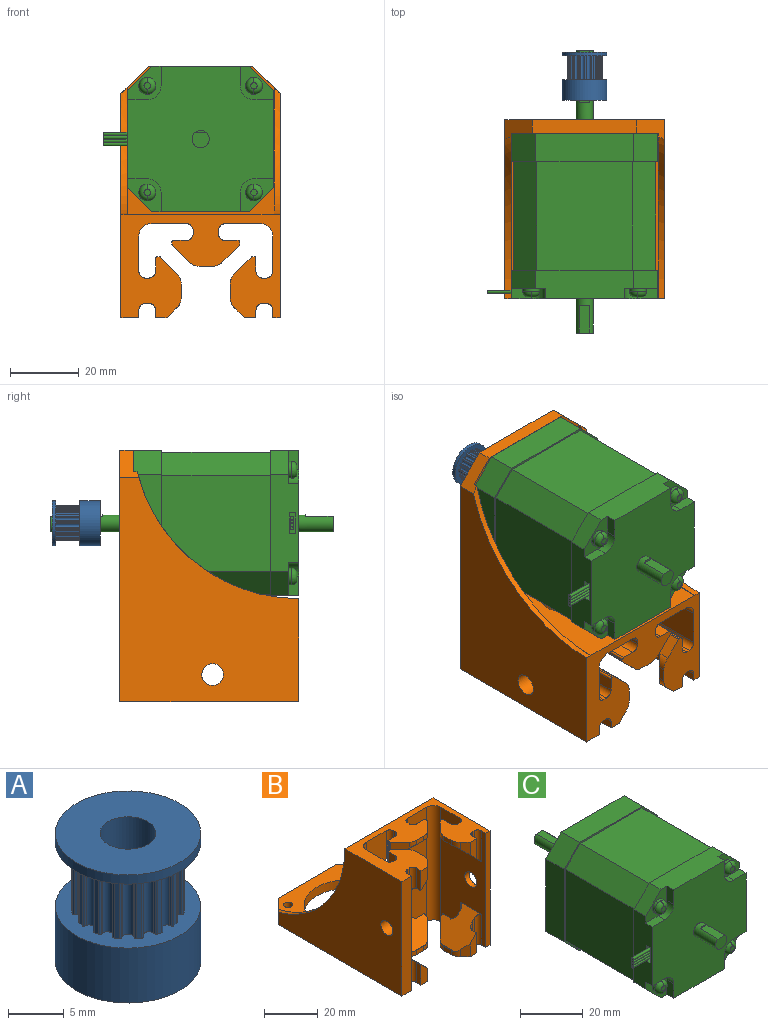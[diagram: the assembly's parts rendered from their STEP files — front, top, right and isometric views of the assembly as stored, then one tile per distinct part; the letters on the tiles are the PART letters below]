
ASSEMBLY  parts=3 mates=2
PART A: 104 faces, bbox 13x13x14 mm
  f0: cylinder r=2.5mm len=14mm, axis (0,0,1), area 214.8mm2, adj f2,f102,f103
  f1: cylinder r=6.5mm len=13mm, axis (0,0,1), area 240.1mm2, adj f2,f3,f103
  f2: plane 13x13mm, normal (0,0,-1), area 113.1mm2, adj f0,f1
  f3: plane 13x13mm, normal (0,0,1), area 62.7mm2, adj f1,f4,f5,f6,f7,f8,f9,f10
  f4: cylinder r=0.15mm len=7mm, axis (0,0,-1), area 1.7mm2, adj f3,f5,f99,f100
  f5: cylinder r=1mm len=7mm, axis (0,0,-1), area 1.7mm2, adj f3,f4,f6,f100
  f6: cylinder r=0.56mm len=7mm, axis (0,0,-1), area 9mm2, adj f3,f5,f7,f100
  f7: cylinder r=1mm len=7mm, axis (0,0,-1), area 1.7mm2, adj f3,f6,f8,f100
  f8: cylinder r=0.15mm len=7mm, axis (0,0,-1), area 1.7mm2, adj f3,f7,f9,f100
  f9: plane 7x0.49mm, normal (0.98,0.2,0), area 3.5mm2, adj f3,f8,f10,f100
  f10: cylinder r=0.15mm len=7mm, axis (0,0,-1), area 1.7mm2, adj f3,f9,f11,f100
  f11: cylinder r=1mm len=7mm, axis (0,0,-1), area 1.7mm2, adj f3,f10,f12,f100
  f12: cylinder r=0.56mm len=7mm, axis (0,0,-1), area 9mm2, adj f3,f11,f13,f100
  f13: cylinder r=1mm len=7mm, axis (0,0,-1), area 1.7mm2, adj f3,f12,f14,f100
  f14: cylinder r=0.15mm len=7mm, axis (0,0,-1), area 1.7mm2, adj f3,f13,f15,f100
  f15: plane 7x0.41mm, normal (0.83,0.56,0), area 3.5mm2, adj f3,f14,f16,f100
  f16: cylinder r=0.15mm len=7mm, axis (0,0,-1), area 1.7mm2, adj f3,f15,f17,f100
  f17: cylinder r=1mm len=7mm, axis (0,0,-1), area 1.7mm2, adj f3,f16,f18,f100
  f18: cylinder r=0.56mm len=7mm, axis (0,0,-1), area 9mm2, adj f3,f17,f19,f100
  f19: cylinder r=1mm len=7mm, axis (0,0,-1), area 1.7mm2, adj f3,f18,f20,f100
  f20: cylinder r=0.15mm len=7mm, axis (0,0,-1), area 1.7mm2, adj f3,f19,f21,f100
  f21: plane 7x0.41mm, normal (0.56,0.83,0), area 3.5mm2, adj f3,f20,f22,f100
  f22: cylinder r=0.15mm len=7mm, axis (0,0,-1), area 1.7mm2, adj f3,f21,f23,f100
  f23: cylinder r=1mm len=7mm, axis (0,0,-1), area 1.7mm2, adj f3,f22,f24,f100
  f24: cylinder r=0.56mm len=7mm, axis (0,0,-1), area 9mm2, adj f3,f23,f25,f100
  f25: cylinder r=1mm len=7mm, axis (0,0,-1), area 1.7mm2, adj f3,f24,f26,f100
  f26: cylinder r=0.15mm len=7mm, axis (0,0,-1), area 1.7mm2, adj f3,f25,f27,f100
  f27: plane 7x0.49mm, normal (0.2,0.98,0), area 3.5mm2, adj f3,f26,f28,f100
  f28: cylinder r=0.15mm len=7mm, axis (0,0,-1), area 1.7mm2, adj f3,f27,f29,f100
  f29: cylinder r=1mm len=7mm, axis (0,0,-1), area 1.7mm2, adj f3,f28,f30,f100
  f30: cylinder r=0.56mm len=7mm, axis (0,0,-1), area 9mm2, adj f3,f29,f31,f100
  f31: cylinder r=1mm len=7mm, axis (0,0,-1), area 1.7mm2, adj f3,f30,f32,f100
  f32: cylinder r=0.15mm len=7mm, axis (0,0,-1), area 1.7mm2, adj f3,f31,f33,f100
  f33: plane 7x0.49mm, normal (-0.2,0.98,0), area 3.5mm2, adj f3,f32,f34,f100
  f34: cylinder r=0.15mm len=7mm, axis (0,0,-1), area 1.7mm2, adj f3,f33,f35,f100
  f35: cylinder r=1mm len=7mm, axis (0,0,-1), area 1.7mm2, adj f3,f34,f36,f100
  f36: cylinder r=0.56mm len=7mm, axis (0,0,-1), area 9mm2, adj f3,f35,f37,f100
  f37: cylinder r=1mm len=7mm, axis (0,0,-1), area 1.7mm2, adj f3,f36,f38,f100
  f38: cylinder r=0.15mm len=7mm, axis (0,0,-1), area 1.7mm2, adj f3,f37,f39,f100
  f39: plane 7x0.41mm, normal (-0.56,0.83,0), area 3.5mm2, adj f3,f38,f40,f100
  f40: cylinder r=0.15mm len=7mm, axis (0,0,-1), area 1.7mm2, adj f3,f39,f41,f100
  f41: cylinder r=1mm len=7mm, axis (0,0,-1), area 1.7mm2, adj f3,f40,f42,f100
  f42: cylinder r=0.56mm len=7mm, axis (0,0,-1), area 9mm2, adj f3,f41,f43,f100
  f43: cylinder r=1mm len=7mm, axis (0,0,-1), area 1.7mm2, adj f3,f42,f44,f100
  f44: cylinder r=0.15mm len=7mm, axis (0,0,-1), area 1.7mm2, adj f3,f43,f45,f100
  f45: plane 7x0.41mm, normal (-0.83,0.56,0), area 3.5mm2, adj f3,f44,f46,f100
  f46: cylinder r=0.15mm len=7mm, axis (0,0,-1), area 1.7mm2, adj f3,f45,f47,f100
  f47: cylinder r=1mm len=7mm, axis (0,0,-1), area 1.7mm2, adj f3,f46,f48,f100
  f48: cylinder r=0.56mm len=7mm, axis (0,0,-1), area 9mm2, adj f3,f47,f49,f100
  f49: cylinder r=1mm len=7mm, axis (0,0,-1), area 1.7mm2, adj f3,f48,f50,f100
  f50: cylinder r=0.15mm len=7mm, axis (0,0,-1), area 1.7mm2, adj f3,f49,f51,f100
  f51: plane 7x0.49mm, normal (-0.98,0.2,0), area 3.5mm2, adj f3,f50,f52,f100
  f52: cylinder r=0.15mm len=7mm, axis (0,0,-1), area 1.7mm2, adj f3,f51,f53,f100
  f53: cylinder r=1mm len=7mm, axis (0,0,-1), area 1.7mm2, adj f3,f52,f54,f100
  f54: cylinder r=0.56mm len=7mm, axis (0,0,-1), area 9mm2, adj f3,f53,f55,f100
  f55: cylinder r=1mm len=7mm, axis (0,0,-1), area 1.7mm2, adj f3,f54,f56,f100
  f56: cylinder r=0.15mm len=7mm, axis (0,0,-1), area 1.7mm2, adj f3,f55,f57,f100
  f57: plane 7x0.49mm, normal (-0.98,-0.2,0), area 3.5mm2, adj f3,f56,f58,f100
  f58: cylinder r=0.15mm len=7mm, axis (0,0,-1), area 1.7mm2, adj f3,f57,f59,f100
  f59: cylinder r=1mm len=7mm, axis (0,0,-1), area 1.7mm2, adj f3,f58,f60,f100
  f60: cylinder r=0.56mm len=7mm, axis (0,0,-1), area 9mm2, adj f3,f59,f61,f100
  f61: cylinder r=1mm len=7mm, axis (0,0,-1), area 1.7mm2, adj f3,f60,f62,f100
  f62: cylinder r=0.15mm len=7mm, axis (0,0,-1), area 1.7mm2, adj f3,f61,f63,f100
  f63: plane 7x0.41mm, normal (-0.83,-0.56,0), area 3.5mm2, adj f3,f62,f64,f100
  f64: cylinder r=0.15mm len=7mm, axis (0,0,-1), area 1.7mm2, adj f3,f63,f65,f100
  f65: cylinder r=1mm len=7mm, axis (0,0,-1), area 1.7mm2, adj f3,f64,f66,f100
  f66: cylinder r=0.56mm len=7mm, axis (0,0,-1), area 9mm2, adj f3,f65,f67,f100
  f67: cylinder r=1mm len=7mm, axis (0,0,-1), area 1.7mm2, adj f3,f66,f68,f100
  f68: cylinder r=0.15mm len=7mm, axis (0,0,-1), area 1.7mm2, adj f3,f67,f69,f100
  f69: plane 7x0.41mm, normal (-0.56,-0.83,0), area 3.5mm2, adj f3,f68,f70,f100
  f70: cylinder r=0.15mm len=7mm, axis (0,0,-1), area 1.7mm2, adj f3,f69,f71,f100
  f71: cylinder r=1mm len=7mm, axis (0,0,-1), area 1.7mm2, adj f3,f70,f72,f100
  f72: cylinder r=0.56mm len=7mm, axis (0,0,-1), area 9mm2, adj f3,f71,f73,f100
  f73: cylinder r=1mm len=7mm, axis (0,0,-1), area 1.7mm2, adj f3,f72,f74,f100
  f74: cylinder r=0.15mm len=7mm, axis (0,0,-1), area 1.7mm2, adj f3,f73,f75,f100
  f75: plane 7x0.49mm, normal (-0.2,-0.98,0), area 3.5mm2, adj f3,f74,f76,f100
  f76: cylinder r=0.15mm len=7mm, axis (0,0,-1), area 1.7mm2, adj f3,f75,f77,f100
  f77: cylinder r=1mm len=7mm, axis (0,0,-1), area 1.7mm2, adj f3,f76,f78,f100
  f78: cylinder r=0.56mm len=7mm, axis (0,0,-1), area 9mm2, adj f3,f77,f79,f100
  f79: cylinder r=1mm len=7mm, axis (0,0,-1), area 1.7mm2, adj f3,f78,f80,f100
  f80: cylinder r=0.15mm len=7mm, axis (0,0,-1), area 1.7mm2, adj f3,f79,f81,f100
  f81: plane 7x0.49mm, normal (0.2,-0.98,0), area 3.5mm2, adj f3,f80,f82,f100
  f82: cylinder r=0.15mm len=7mm, axis (0,0,-1), area 1.7mm2, adj f3,f81,f83,f100
  f83: cylinder r=1mm len=7mm, axis (0,0,-1), area 1.7mm2, adj f3,f82,f84,f100
  f84: cylinder r=0.56mm len=7mm, axis (0,0,-1), area 9mm2, adj f3,f83,f85,f100
  f85: cylinder r=1mm len=7mm, axis (0,0,-1), area 1.7mm2, adj f3,f84,f86,f100
  f86: cylinder r=0.15mm len=7mm, axis (0,0,-1), area 1.7mm2, adj f3,f85,f87,f100
  f87: plane 7x0.41mm, normal (0.56,-0.83,0), area 3.5mm2, adj f3,f86,f88,f100
  f88: cylinder r=0.15mm len=7mm, axis (0,0,-1), area 1.7mm2, adj f3,f87,f89,f100
  f89: cylinder r=1mm len=7mm, axis (0,0,-1), area 1.7mm2, adj f3,f88,f90,f100
  f90: cylinder r=0.56mm len=7mm, axis (0,0,-1), area 9mm2, adj f3,f89,f91,f100
  f91: cylinder r=1mm len=7mm, axis (0,0,-1), area 1.7mm2, adj f3,f90,f92,f100
  f92: cylinder r=0.15mm len=7mm, axis (0,0,-1), area 1.7mm2, adj f3,f91,f93,f100
  f93: plane 7x0.41mm, normal (0.83,-0.56,0), area 3.5mm2, adj f3,f92,f94,f100
  f94: cylinder r=0.15mm len=7mm, axis (0,0,-1), area 1.7mm2, adj f3,f93,f95,f100
  f95: cylinder r=1mm len=7mm, axis (0,0,-1), area 1.7mm2, adj f3,f94,f96,f100
  f96: cylinder r=0.56mm len=7mm, axis (0,0,-1), area 9mm2, adj f3,f95,f97,f100
  f97: cylinder r=1mm len=7mm, axis (0,0,-1), area 1.7mm2, adj f3,f96,f98,f100
  f98: cylinder r=0.15mm len=7mm, axis (0,0,-1), area 1.7mm2, adj f3,f97,f99,f100
  f99: plane 7x0.49mm, normal (0.98,-0.2,0), area 3.5mm2, adj f3,f4,f98,f100
  f100: plane 13x13mm, normal (0,0,-1), area 62.7mm2, adj f4,f5,f6,f7,f8,f9,f10,f11
  f101: cylinder r=6.5mm len=13mm, axis (0,0,-1), area 40.8mm2, adj f100,f102
  f102: plane 13x13mm, normal (0,0,1), area 113.1mm2, adj f0,f101
  f103: cylinder r=1.25mm len=4.34mm, axis (0,-1,0), area 32.2mm2, adj f0,f1
PART B: 154 faces, bbox 46.4x73.1x52.1 mm
  f0: plane 52x10.23mm, normal (0,-1,0), area 397.5mm2, adj f41,f42,f43,f111,f125,f144,f145,f148
  f1: plane 9.14x3.34mm, normal (0,-1,0), area 24.9mm2, adj f91,f101,f111,f137
  f2: plane 9.14x3.34mm, normal (0,-1,0), area 24.9mm2, adj f92,f102,f125,f139
  f3: plane 9.14x3.34mm, normal (0,-1,0), area 24.9mm2, adj f89,f99,f111,f136
  f4: plane 9.14x3.34mm, normal (0,-1,0), area 24.9mm2, adj f90,f100,f125,f141
  f5: cylinder r=1.95mm len=14mm, axis (0,0,-1), area 40.8mm2, adj f7,f111,f117,f138
  f6: cylinder r=1.95mm len=14mm, axis (0,0,-1), area 40.8mm2, adj f8,f117,f125,f140
  f7: plane 12.05x0.96mm, normal (1,0,0), area 11.1mm2, adj f5,f9,f111,f138
  f8: plane 12.05x0.96mm, normal (1,0,0), area 11.1mm2, adj f6,f10,f125,f140
  f9: cylinder r=1.95mm len=11.09mm, axis (0,0,-1), area 30.2mm2, adj f7,f11,f111,f138
  f10: cylinder r=1.95mm len=11.09mm, axis (0,0,-1), area 30.2mm2, adj f8,f12,f125,f140
  f11: plane 9.14x3.77mm, normal (0,1,0), area 34.4mm2, adj f9,f13,f111,f138
  f12: plane 9.14x3.77mm, normal (0,1,0), area 34.4mm2, adj f10,f14,f125,f140
  f13: cylinder r=0.5mm len=9.14mm, axis (0,0,-1), area 7.1mm2, adj f11,f15,f111,f138
  f14: cylinder r=0.5mm len=9.14mm, axis (0,0,-1), area 7.1mm2, adj f12,f16,f125,f140
  f15: plane 8.63x0.53mm, normal (1,0,0), area 4.5mm2, adj f13,f17,f111,f138
  f16: plane 8.63x0.53mm, normal (1,0,0), area 4.5mm2, adj f14,f18,f125,f140
  f17: cylinder r=0.5mm len=8.1mm, axis (0,0,-1), area 3.1mm2, adj f15,f19,f111,f138
  f18: cylinder r=0.5mm len=8.1mm, axis (0,0,-1), area 3.1mm2, adj f16,f20,f125,f140
  f19: plane 7.75x5.05mm, normal (0.71,-0.71,0), area 37.3mm2, adj f17,f21,f111,f138
  f20: plane 7.75x5.05mm, normal (0.71,-0.71,0), area 37.3mm2, adj f18,f22,f125,f140
  f21: cylinder r=4.36mm len=2.78mm, axis (0,0,-1), area 6.5mm2, adj f19,f23,f111,f134,f138
  f22: cylinder r=4.36mm len=2.78mm, axis (0,0,-1), area 6.5mm2, adj f20,f24,f125,f135,f140
  f23: plane 3.8x2mm, normal (0,-1,0), area 7.6mm2, adj f21,f25,f111,f134
  f24: plane 3.8x2mm, normal (0,-1,0), area 7.6mm2, adj f22,f26,f125,f135
  f25: cylinder r=4.36mm len=2.78mm, axis (0,0,-1), area 6.5mm2, adj f23,f27,f111,f134,f138
  f26: cylinder r=4.36mm len=2.78mm, axis (0,0,-1), area 6.5mm2, adj f24,f28,f125,f135,f140
  f27: plane 7.75x5.05mm, normal (-0.71,-0.71,0), area 37.3mm2, adj f25,f29,f111,f138
  f28: plane 7.75x5.05mm, normal (-0.71,-0.71,0), area 37.3mm2, adj f26,f30,f125,f140
  f29: cylinder r=0.5mm len=8.1mm, axis (0,0,-1), area 3.1mm2, adj f27,f31,f111,f138
  f30: cylinder r=0.5mm len=8.1mm, axis (0,0,-1), area 3.1mm2, adj f28,f32,f125,f140
  f31: plane 8.63x0.53mm, normal (-1,0,0), area 4.5mm2, adj f29,f33,f111,f138
  f32: plane 8.63x0.53mm, normal (-1,0,0), area 4.5mm2, adj f30,f34,f125,f140
  f33: cylinder r=0.5mm len=9.14mm, axis (0,0,-1), area 7.1mm2, adj f31,f35,f111,f138
  f34: cylinder r=0.5mm len=9.14mm, axis (0,0,-1), area 7.1mm2, adj f32,f36,f125,f140
  f35: plane 9.14x3.77mm, normal (0,1,0), area 34.4mm2, adj f33,f37,f111,f138
  f36: plane 9.14x3.77mm, normal (0,1,0), area 34.4mm2, adj f34,f38,f125,f140
  f37: cylinder r=1.95mm len=11.09mm, axis (0,0,-1), area 30.2mm2, adj f35,f39,f111,f138
  f38: cylinder r=1.95mm len=11.09mm, axis (0,0,-1), area 30.2mm2, adj f36,f40,f125,f140
  f39: plane 12.05x0.96mm, normal (-1,0,0), area 11.1mm2, adj f37,f41,f111,f138
  f40: plane 11.18x0.96mm, normal (-1,0,0), area 10.7mm2, adj f38,f42,f125,f140,f149
  f41: cylinder r=1.95mm len=13.8mm, axis (0,0,-1), area 38.8mm2, adj f0,f39,f111,f138,f144,f151
  f42: cylinder r=1.95mm len=12.8mm, axis (0,0,-1), area 35.8mm2, adj f0,f40,f125,f145,f149
  f43: cylinder r=3.49mm len=52mm, axis (0,0,-1), area 296.8mm2, adj f0,f111,f118,f125
  f44: cylinder r=1.95mm len=14mm, axis (0,0,-1), area 40.8mm2, adj f46,f111,f118,f136
  f45: cylinder r=1.95mm len=14mm, axis (0,0,-1), area 40.8mm2, adj f47,f118,f125,f141
  f46: plane 12.05x0.96mm, normal (0,1,0), area 11.1mm2, adj f44,f48,f111,f136
  f47: plane 12.05x0.96mm, normal (0,1,0), area 11.1mm2, adj f45,f49,f125,f141
  f48: cylinder r=1.95mm len=11.09mm, axis (0,0,-1), area 30.2mm2, adj f46,f50,f111,f136
  f49: cylinder r=1.95mm len=11.09mm, axis (0,0,-1), area 30.2mm2, adj f47,f51,f125,f141
  f50: plane 9.14x3.77mm, normal (-1,0,0), area 34.4mm2, adj f48,f52,f111,f136
  f51: plane 9.14x3.77mm, normal (-1,0,0), area 34.4mm2, adj f49,f53,f125,f141
  f52: cylinder r=0.5mm len=9.14mm, axis (0,0,-1), area 7.1mm2, adj f50,f54,f111,f136
  f53: cylinder r=0.5mm len=9.14mm, axis (0,0,-1), area 7.1mm2, adj f51,f55,f125,f141
  f54: plane 8.63x0.57mm, normal (0,1,0), area 4.7mm2, adj f52,f56,f111,f136
  f55: plane 8.63x0.57mm, normal (0,1,0), area 4.7mm2, adj f53,f57,f125,f141
  f56: cylinder r=0.5mm len=8.07mm, axis (0,0,-1), area 3.1mm2, adj f54,f58,f111,f136
  f57: cylinder r=0.5mm len=8.07mm, axis (0,0,-1), area 3.1mm2, adj f55,f59,f125,f141
  f58: plane 7.71x5.01mm, normal (0.71,0.71,0), area 36.9mm2, adj f56,f60,f111,f136
  f59: plane 7.71x5.01mm, normal (0.71,0.71,0), area 36.9mm2, adj f57,f61,f125,f141
  f60: cylinder r=4.37mm len=2.79mm, axis (0,0,-1), area 6.5mm2, adj f58,f62,f111,f132,f136
  f61: cylinder r=4.37mm len=2.79mm, axis (0,0,-1), area 6.5mm2, adj f59,f63,f125,f133,f141
  f62: plane 3.87x2mm, normal (1,0,0), area 7.7mm2, adj f60,f64,f111,f132
  f63: plane 3.87x2mm, normal (1,0,0), area 7.7mm2, adj f61,f65,f125,f133
  f64: cylinder r=4.37mm len=3.36mm, axis (0,0,-1), area 8.9mm2, adj f62,f89,f111,f132,f136
  f65: cylinder r=4.37mm len=3.36mm, axis (0,0,-1), area 8.9mm2, adj f63,f90,f125,f133,f141
  f66: cylinder r=4.37mm len=3.36mm, axis (0,0,-1), area 8.9mm2, adj f68,f91,f111,f130,f137
  f67: cylinder r=4.37mm len=3.36mm, axis (0,0,-1), area 8.9mm2, adj f69,f92,f125,f131,f139
  f68: plane 3.87x2mm, normal (-1,0,0), area 7.7mm2, adj f66,f70,f111,f130
  f69: plane 3.87x2mm, normal (-1,0,0), area 7.7mm2, adj f67,f71,f125,f131
  f70: cylinder r=4.37mm len=3.36mm, axis (0,0,-1), area 8.9mm2, adj f68,f72,f111,f130,f137
  f71: cylinder r=4.37mm len=3.36mm, axis (0,0,-1), area 8.9mm2, adj f69,f73,f125,f131,f139
  f72: plane 7.71x4.45mm, normal (-0.71,0.71,0), area 34.5mm2, adj f70,f74,f111,f137
  f73: plane 7.71x4.45mm, normal (-0.71,0.71,0), area 34.5mm2, adj f71,f75,f125,f139
  f74: cylinder r=0.5mm len=8.07mm, axis (0,0,-1), area 3.1mm2, adj f72,f76,f111,f137
  f75: cylinder r=0.5mm len=8.07mm, axis (0,0,-1), area 3.1mm2, adj f73,f77,f125,f139
  f76: plane 8.63x0.57mm, normal (0,1,0), area 4.7mm2, adj f74,f78,f111,f137
  f77: plane 8.63x0.57mm, normal (0,1,0), area 4.7mm2, adj f75,f79,f125,f139
  f78: cylinder r=0.5mm len=9.14mm, axis (0,0,-1), area 7.1mm2, adj f76,f80,f111,f137
  f79: cylinder r=0.5mm len=9.14mm, axis (0,0,-1), area 7.1mm2, adj f77,f81,f125,f139
  f80: plane 9.14x3.77mm, normal (1,0,0), area 34.4mm2, adj f78,f82,f111,f137
  f81: plane 9.14x3.77mm, normal (1,0,0), area 34.4mm2, adj f79,f83,f125,f139
  f82: cylinder r=1.95mm len=11.09mm, axis (0,0,-1), area 30.2mm2, adj f80,f84,f111,f137
  f83: cylinder r=1.95mm len=11.09mm, axis (0,0,-1), area 30.2mm2, adj f81,f85,f125,f139
  f84: plane 12.05x0.96mm, normal (0,1,0), area 11.1mm2, adj f82,f86,f111,f137
  f85: plane 12.05x0.96mm, normal (0,1,0), area 11.1mm2, adj f83,f87,f125,f139
  f86: cylinder r=1.95mm len=14mm, axis (0,0,-1), area 40.8mm2, adj f84,f111,f119,f137
  f87: cylinder r=1.95mm len=14mm, axis (0,0,-1), area 40.8mm2, adj f85,f119,f125,f139
  f88: cylinder r=3.49mm len=52mm, axis (0,0,-1), area 296.8mm2, adj f111,f117,f119,f125
  f89: plane 5.8x2.53mm, normal (0.71,-0.71,0), area 16.2mm2, adj f3,f64,f111,f136
  f90: plane 5.8x2.53mm, normal (0.71,-0.71,0), area 16.2mm2, adj f4,f65,f125,f141
  f91: plane 5.8x2.53mm, normal (-0.71,-0.71,0), area 16.2mm2, adj f1,f66,f111,f137
  f92: plane 5.8x2.53mm, normal (-0.71,-0.71,0), area 16.2mm2, adj f2,f67,f125,f139
  f93: cylinder r=1.95mm len=11.09mm, axis (0,0,-1), area 30.2mm2, adj f95,f99,f111,f136
  f94: cylinder r=1.95mm len=11.09mm, axis (0,0,-1), area 30.2mm2, adj f96,f100,f125,f141
  f95: plane 12.05x0.96mm, normal (0,-1,0), area 11.1mm2, adj f93,f97,f111,f136
  f96: plane 12.05x0.96mm, normal (0,-1,0), area 11.1mm2, adj f94,f98,f125,f141
  f97: cylinder r=1.95mm len=14mm, axis (0,0,-1), area 40.8mm2, adj f95,f111,f118,f136
  f98: cylinder r=1.95mm len=14mm, axis (0,0,-1), area 40.8mm2, adj f96,f118,f125,f141
  f99: plane 9.14x2.21mm, normal (-1,0,0), area 20.2mm2, adj f3,f93,f111,f136
  f100: plane 9.14x2.21mm, normal (-1,0,0), area 20.2mm2, adj f4,f94,f125,f141
  f101: plane 9.14x2.21mm, normal (1,0,0), area 20.2mm2, adj f1,f103,f111,f137
  f102: plane 9.14x2.21mm, normal (1,0,0), area 20.2mm2, adj f2,f104,f125,f139
  f103: cylinder r=1.95mm len=11.09mm, axis (0,0,-1), area 30.2mm2, adj f101,f105,f111,f137
  f104: cylinder r=1.95mm len=11.09mm, axis (0,0,-1), area 30.2mm2, adj f102,f106,f125,f139
  f105: plane 12.05x0.96mm, normal (0,-1,0), area 11.1mm2, adj f103,f107,f111,f137
  f106: plane 12.05x0.96mm, normal (0,-1,0), area 11.1mm2, adj f104,f108,f125,f139
  f107: cylinder r=1.95mm len=14mm, axis (0,0,-1), area 40.8mm2, adj f105,f111,f119,f137
  f108: cylinder r=1.95mm len=14mm, axis (0,0,-1), area 40.8mm2, adj f106,f119,f125,f139
  f109: plane 48x42.7mm, normal (0,1,0), area 1547.3mm2, adj f110,f125,f127,f129,f144,f145,f146,f147
  f110: plane 43.08x42.7mm, normal (0,0,1), area 960.3mm2, adj f109,f115,f120,f121,f122,f123,f124,f127
  f111: plane 73x46.3mm, normal (0,0,-1), area 1851.5mm2, adj f0,f1,f3,f5,f7,f9,f11,f13
  f112: plane 52x2.2mm, normal (0,-1,0), area 114.4mm2, adj f111,f114,f119,f125
  f113: plane 52x5.2mm, normal (0,-1,0), area 270.4mm2, adj f111,f116,f118,f125
  f114: plane 65x52mm, normal (1,0,0), area 2147mm2, adj f111,f112,f125,f126,f143,f152
  f115: plane 30.3x4mm, normal (0,1,0), area 121.2mm2, adj f110,f111,f142,f143
  f116: plane 65x52mm, normal (-1,0,0), area 2147mm2, adj f111,f113,f125,f128,f142,f153
  f117: plane 52x13.06mm, normal (0,-1,0), area 470.1mm2, adj f5,f6,f88,f111,f125,f138,f140,f146
  f118: plane 52x23.67mm, normal (1,0,0), area 884.7mm2, adj f43,f44,f45,f97,f98,f111,f113,f125
  f119: plane 52x23.67mm, normal (-1,0,0), area 884.7mm2, adj f86,f87,f88,f107,f108,f111,f112,f125
  f120: cylinder r=16mm len=32mm, axis (0,0,1), area 402.1mm2, adj f110,f111
  f121: cylinder r=1.7mm len=4mm, axis (0,0,1), area 42.7mm2, adj f110,f111
  f122: cylinder r=1.7mm len=4mm, axis (0,0,1), area 42.7mm2, adj f110,f111
  f123: cylinder r=1.7mm len=4mm, axis (0,0,1), area 42.7mm2, adj f110,f111
  f124: cylinder r=1.7mm len=4mm, axis (0,0,1), area 42.7mm2, adj f110,f111
  f125: plane 46.3x29.92mm, normal (0,0,1), area 761.6mm2, adj f0,f2,f4,f6,f8,f10,f12,f14
  f126: cylinder r=48.28mm len=46.92mm, axis (1,0,0), area 114.1mm2, adj f114,f125,f127,f143
  f127: plane 48x36.88mm, normal (-1,0,0), area 484.7mm2, adj f109,f110,f126,f143
  f128: cylinder r=48.28mm len=46.92mm, axis (-1,0,0), area 114.1mm2, adj f116,f125,f129,f142
  f129: plane 48x36.88mm, normal (1,0,0), area 484.7mm2, adj f109,f110,f128,f142
  f130: plane 7.11x0.31mm, normal (0,0,1), area 1.9mm2, adj f66,f68,f70,f137
  f131: plane 7.11x0.31mm, normal (0,0,-1), area 1.9mm2, adj f67,f69,f71,f139
  f132: plane 7.11x0.31mm, normal (0,0,1), area 1.9mm2, adj f60,f62,f64,f136
  f133: plane 7.11x0.31mm, normal (0,0,-1), area 1.9mm2, adj f61,f63,f65,f141
  f134: plane 7.04x0.31mm, normal (0,0,1), area 1.9mm2, adj f21,f23,f25,f138
  f135: plane 7.04x0.31mm, normal (0,0,-1), area 1.9mm2, adj f22,f24,f26,f140
  f136: plane 17.8x12.09mm, normal (0.71,0,0.71), area 198.9mm2, adj f3,f44,f46,f48,f50,f52,f54,f56
  f137: plane 17.74x12.03mm, normal (-0.71,0,0.71), area 198.9mm2, adj f1,f66,f70,f72,f74,f76,f78,f80
  f138: plane 19.87x12.09mm, normal (0,-0.71,0.71), area 187.4mm2, adj f5,f7,f9,f11,f13,f15,f17,f19
  f139: plane 17.74x12.03mm, normal (-0.71,0,-0.71), area 198.9mm2, adj f2,f67,f71,f73,f75,f77,f79,f81
  f140: plane 19.87x12.09mm, normal (0,-0.71,-0.71), area 177.7mm2, adj f6,f8,f10,f12,f14,f16,f18,f20
  f141: plane 17.8x12.09mm, normal (0.71,0,-0.71), area 198.9mm2, adj f4,f45,f47,f49,f51,f53,f55,f57
  f142: plane 8x8mm, normal (-0.71,0.71,0), area 48.6mm2, adj f110,f111,f115,f116,f128,f129
  f143: plane 8x8mm, normal (0.71,0.71,0), area 48.6mm2, adj f110,f111,f114,f115,f126,f127
  f144: plane 9.82x8.42mm, normal (0.76,0,0.65), area 34.3mm2, adj f0,f41,f109,f148,f151
  f145: plane 9.82x8.42mm, normal (0.76,0,-0.65), area 34.3mm2, adj f0,f42,f109,f148,f149
  f146: plane 9.82x8.41mm, normal (-0.76,0,-0.65), area 35.9mm2, adj f109,f117,f140,f149,f150
  f147: plane 9.82x8.41mm, normal (-0.76,0,0.65), area 34.5mm2, adj f109,f117,f138,f150,f151
  f148: cylinder r=5mm len=6.51mm, axis (0,-1,0), area 18.8mm2, adj f0,f109,f144,f145
  f149: cylinder r=5mm len=7.59mm, axis (0,-1,0), area 42.6mm2, adj f40,f42,f109,f140,f145,f146
  f150: cylinder r=5mm len=6.51mm, axis (0,-1,0), area 18.8mm2, adj f109,f117,f146,f147
  f151: cylinder r=5mm len=7.59mm, axis (0,-1,0), area 36mm2, adj f41,f109,f138,f144,f147
  f152: cylinder r=3.17mm len=6.35mm, axis (-1,0,0), area 43.9mm2, adj f114,f119
  f153: cylinder r=3.17mm len=6.35mm, axis (-1,0,0), area 103.7mm2, adj f116,f118
PART C: 93 faces, bbox 49.3x82x42.3 mm
  f0: plane 42.3x42.3mm, normal (0,1,0), area 858.8mm2, adj f1,f13,f15,f17,f19,f21,f32,f34
  f1: plane 8.25x7mm, normal (0.71,0,0.71), area 81.7mm2, adj f0,f3,f21,f34
  f2: plane 7x7mm, normal (0.71,0,0.71), area 52mm2, adj f12,f22,f23,f35
  f3: plane 42.3x42.3mm, normal (0,-1,0), area 75.6mm2, adj f1,f4,f5,f6,f7,f8,f9,f10
  f4: plane 31.5x6.71mm, normal (0.71,0,0.71), area 298.8mm2, adj f3,f5,f11,f12
  f5: plane 31.5x27.89mm, normal (1,0,0), area 878.4mm2, adj f3,f4,f6,f12
  f6: plane 31.5x6.71mm, normal (0.71,0,-0.71), area 298.8mm2, adj f3,f5,f7,f12
  f7: plane 31.5x27.89mm, normal (0,0,-1), area 878.4mm2, adj f3,f6,f8,f12
  f8: plane 31.5x6.71mm, normal (-0.71,0,-0.71), area 298.8mm2, adj f3,f7,f9,f12
  f9: plane 31.5x27.89mm, normal (-1,0,0), area 878.4mm2, adj f3,f8,f10,f12
  f10: plane 31.5x6.71mm, normal (-0.71,0,0.71), area 298.8mm2, adj f3,f9,f11,f12
  f11: plane 31.5x27.89mm, normal (0,0,1), area 878.4mm2, adj f3,f4,f10,f12
  f12: plane 42.3x42.3mm, normal (0,1,0), area 75.6mm2, adj f2,f4,f5,f6,f7,f8,f9,f10
  f13: plane 28.3x8.25mm, normal (-1,0,0), area 233.5mm2, adj f0,f3,f15,f32
  f14: plane 28.3x8.25mm, normal (-1,0,0), area 207.1mm2, adj f12,f16,f27,f29,f31,f33,f49,f50
  f15: plane 8.25x7mm, normal (-0.71,0,-0.71), area 81.7mm2, adj f0,f3,f13,f17
  f16: plane 7x7mm, normal (-0.71,0,-0.71), area 52mm2, adj f12,f14,f18,f49
  f17: plane 28.3x8.25mm, normal (0,0,-1), area 233.5mm2, adj f0,f3,f15,f19
  f18: plane 28.3x8.25mm, normal (0,0,-1), area 217.6mm2, adj f12,f16,f20,f27,f41,f42,f48,f49
  f19: plane 8.25x7mm, normal (0.71,0,-0.71), area 81.7mm2, adj f0,f3,f17,f21
  f20: plane 7x7mm, normal (0.71,0,-0.71), area 52mm2, adj f12,f18,f22,f41
  f21: plane 28.3x8.25mm, normal (1,0,0), area 233.5mm2, adj f0,f1,f3,f19
  f22: plane 28.3x8.25mm, normal (1,0,0), area 217.6mm2, adj f2,f12,f20,f23,f26,f27,f40,f41
  f23: plane 9.65x9.65mm, normal (0,-1,0), area 46.4mm2, adj f2,f22,f24,f25,f26,f35,f60
  f24: plane 5.65x3mm, normal (1,0,0), area 17mm2, adj f23,f25,f27,f35
  f25: cylinder r=4mm len=4mm, axis (0,1,0), area 18.8mm2, adj f23,f24,f26,f27
  f26: plane 5.65x3mm, normal (0,0,1), area 17mm2, adj f22,f23,f25,f27
  f27: plane 42.3x42.3mm, normal (0,-1,0), area 1410.9mm2, adj f14,f18,f22,f24,f25,f26,f28,f30
  f28: plane 5.65x3mm, normal (-1,0,0), area 17mm2, adj f27,f29,f30,f35
  f29: plane 9.65x9.65mm, normal (0,-1,0), area 46.4mm2, adj f14,f28,f30,f31,f33,f35,f36
  f30: cylinder r=4mm len=4mm, axis (0,-1,0), area 18.8mm2, adj f27,f28,f29,f31
  f31: plane 5.65x3mm, normal (0,0,1), area 17mm2, adj f14,f27,f29,f30
  f32: plane 8.25x7mm, normal (-0.71,0,0.71), area 81.7mm2, adj f0,f3,f13,f34
  f33: plane 7x7mm, normal (-0.71,0,0.71), area 52mm2, adj f12,f14,f29,f35
  f34: plane 28.3x8.25mm, normal (0,0,1), area 233.5mm2, adj f0,f1,f3,f32
  f35: plane 28.3x8.25mm, normal (0,0,1), area 217.6mm2, adj f2,f12,f23,f24,f27,f28,f29,f33
  f36: cylinder r=2.45mm len=4.9mm, axis (0,-1,0), area 15.4mm2, adj f29,f37,f39
  f37: torus R=0.95mm, axis (0,-1,0), area 14.1mm2, adj f36,f38,f39
  f38: plane 1.9x1.9mm, normal (0,-1,0), area 2.8mm2, adj f37,f39
  f39: torus R=0.95mm, axis (0,-1,0), area 14.1mm2, adj f36,f37,f38
  f40: plane 5.65x3mm, normal (0,0,-1), area 17mm2, adj f22,f27,f41,f43
  f41: plane 9.65x9.65mm, normal (0,-1,0), area 46.4mm2, adj f18,f20,f22,f40,f42,f43,f44
  f42: plane 5.65x3mm, normal (1,0,0), area 17mm2, adj f18,f27,f41,f43
  f43: cylinder r=4mm len=4mm, axis (0,-1,0), area 18.8mm2, adj f27,f40,f41,f42
  f44: cylinder r=2.45mm len=4.9mm, axis (0,-1,0), area 15.4mm2, adj f41,f45,f47
  f45: torus R=0.95mm, axis (0,-1,0), area 14.1mm2, adj f44,f46,f47
  f46: plane 1.9x1.9mm, normal (0,-1,0), area 2.8mm2, adj f45,f47
  f47: torus R=0.95mm, axis (0,-1,0), area 14.1mm2, adj f44,f45,f46
  f48: plane 5.65x3mm, normal (-1,0,0), area 17mm2, adj f18,f27,f49,f51
  f49: plane 9.65x9.65mm, normal (0,-1,0), area 46.4mm2, adj f14,f16,f18,f48,f50,f51,f52
  f50: plane 5.65x3mm, normal (0,0,-1), area 17mm2, adj f14,f27,f49,f51
  f51: cylinder r=4mm len=4mm, axis (0,1,0), area 18.8mm2, adj f27,f48,f49,f50
  f52: cylinder r=2.45mm len=4.9mm, axis (0,1,0), area 15.4mm2, adj f49,f53,f55
  f53: torus R=0.95mm, axis (0,1,0), area 14.1mm2, adj f52,f54,f55
  f54: plane 1.9x1.9mm, normal (0,-1,0), area 2.8mm2, adj f53,f55
  f55: torus R=0.95mm, axis (0,1,0), area 14.1mm2, adj f52,f53,f54
  f56: cylinder r=2.5mm len=10mm, axis (0,-1,0), area 131.3mm2, adj f27,f57,f58,f59
  f57: plane 8x3mm, normal (0,0,1), area 24mm2, adj f56,f58,f59
  f58: plane 5x4.5mm, normal (0,-1,0), area 18.6mm2, adj f56,f57
  f59: plane 3x0.5mm, normal (0,-1,0), area 1mm2, adj f56,f57
  f60: cylinder r=2.45mm len=4.9mm, axis (0,1,0), area 15.4mm2, adj f23,f61,f63
  f61: torus R=0.95mm, axis (0,1,0), area 14.1mm2, adj f60,f62,f63
  f62: plane 1.9x1.9mm, normal (0,-1,0), area 2.8mm2, adj f61,f63
  f63: torus R=0.95mm, axis (0,1,0), area 14.1mm2, adj f60,f61,f62
  f64: plane 3x1.75mm, normal (0,0,1), area 5.3mm2, adj f14,f65,f67,f68
  f65: plane 6x3mm, normal (0,-1,0), area 18mm2, adj f14,f64,f66,f68
  f66: plane 3x1.75mm, normal (0,0,-1), area 5.3mm2, adj f14,f65,f67,f68
  f67: plane 6x3mm, normal (0,1,0), area 18mm2, adj f14,f64,f66,f68
  f68: plane 6x1.75mm, normal (-1,0,0), area 7.6mm2, adj f64,f65,f66,f67,f69,f71,f73,f75
  f69: cylinder r=0.48mm len=10mm, axis (-1,0,0), area 30mm2, adj f68,f70
  f70: plane 0.96x0.96mm, normal (-1,0,0), area 0.7mm2, adj f69
  f71: cylinder r=0.48mm len=10mm, axis (-1,0,0), area 30mm2, adj f68,f72
  f72: plane 0.96x0.96mm, normal (-1,0,0), area 0.7mm2, adj f71
  f73: cylinder r=0.48mm len=10mm, axis (-1,0,0), area 30mm2, adj f68,f74
  f74: plane 0.96x0.96mm, normal (-1,0,0), area 0.7mm2, adj f73
  f75: cylinder r=0.48mm len=10mm, axis (-1,0,0), area 30mm2, adj f68,f76
  f76: plane 0.96x0.96mm, normal (-1,0,0), area 0.7mm2, adj f75
  f77: cylinder r=1.5mm len=4.5mm, axis (0,-1,0), area 42.4mm2, adj f0,f78
  f78: plane 3x3mm, normal (0,1,0), area 7.1mm2, adj f77
  f79: cylinder r=1.5mm len=4.5mm, axis (0,1,0), area 42.4mm2, adj f0,f80
  f80: plane 3x3mm, normal (0,1,0), area 7.1mm2, adj f79
  f81: cylinder r=1.5mm len=4.5mm, axis (0,1,0), area 42.4mm2, adj f0,f82
  f82: plane 3x3mm, normal (0,1,0), area 7.1mm2, adj f81
  f83: cylinder r=1.5mm len=4.5mm, axis (0,-1,0), area 42.4mm2, adj f0,f84
  f84: plane 3x3mm, normal (0,1,0), area 7.1mm2, adj f83
  f85: cylinder r=16mm len=32mm, axis (0,1,0), area 40.2mm2, adj f0,f86
  f86: plane 32x32mm, normal (0,1,0), area 424.1mm2, adj f85,f87
  f87: cylinder r=11mm len=22mm, axis (0,1,0), area 165.9mm2, adj f86,f88
  f88: plane 22x22mm, normal (0,1,0), area 360.5mm2, adj f87,f89
  f89: cylinder r=2.5mm len=22mm, axis (0,1,0), area 297.3mm2, adj f88,f90,f91,f92
  f90: plane 3x0.5mm, normal (0,1,0), area 1mm2, adj f89,f91
  f91: plane 15x3mm, normal (0,0,1), area 45mm2, adj f89,f90,f92
  f92: plane 5x4.5mm, normal (0,1,0), area 18.6mm2, adj f89,f91
PLACE A rot(axis=(-0.82,-0.41,-0.41),101.4deg) t=(-31.56,26.88,0.34)mm
PLACE B rot(axis=(1,0,0),90deg) t=(-31.56,15.26,-2.66)mm
PLACE C t=(-31.56,11.26,0.34)mm fixed
MATE revolute A.f0 <-> C.f56  axis (0,-1,0) through (-31.56,20.88,0.34)mm
MATE fastened C.f56 <-> B.f120  axis (0,1,0) through (-31.56,11.26,0.34)mm
